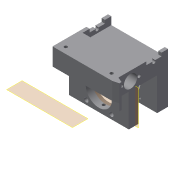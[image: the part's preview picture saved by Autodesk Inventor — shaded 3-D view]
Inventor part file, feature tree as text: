
AUTODESK INVENTOR PART (.ipt)
format: ipt  version: 2019.4 (Build 234330000, 330)  size: 334,848 bytes
history: native  units: mm
features: sketch x14, extrude x10, projected_geometry x9, hole x5, plane x4, other x3
ambient origin geometry x8: Origin, YZ Plane, XZ Plane, XY Plane, X Axis, Y Axis, Z Axis, Center Point
bodies: Body1 (feature_tree)
feature tree (45):
  plane  "Work Plane5"
  extrude  "Extrusion7"  Depth=16.0mm TaperAngle=0.0deg
  extrude  "Extrusion8"  Depth=4.0mm
  hole  "Hole1"  [1 undecoded]
  extrude  "Extrusion9"  Depth=6.2mm
  extrude  "Extrusion12"  Depth=10.0mm TaperAngle=0.0deg
  hole  "Hole4"  [1 undecoded]
  plane  "Work Plane8"
  extrude  "Extrusion13"  Depth=6.0mm
  extrude  "Extrusion18"  Depth=0.3mm
  extrude  "Extrusion19"  Depth=4.0mm
  extrude  "Extrusion20"  Depth=1.0mm
  hole  "Hole5"  [1 undecoded]
  hole  "Hole7"  [1 undecoded]
  hole  "Hole8"  [1 undecoded]
  sketch  "Sketch30"  dims[d122=6.9mm d123=2.0mm d124=0.0mm]
  plane  "Work Plane9"
  extrude  "Extrusion21"  Depth=10.0mm
  sketch  "Sketch31"  dims[d125=3.0mm d126=0.0mm d127=2.8mm d128=6.0mm d129=19.05mm d130=4.775mm d131=90.0deg d132=8.0mm d133=20.594885mm d143=4.0mm d144=6.0mm d145=19.05mm d146=4.775mm d147=90.0deg d148=8.0mm d149=20.594885mm d150=2.8mm d151=2.8mm d152=45.0mm d153=25.0mm d154=2.8mm d155=6.0mm d156=19.05mm d157=4.775mm d158=90.0deg d159=8.0mm d160=20.594885mm d161=5.0mm d162=2.0mm d163=10.0mm d164=0.0mm d165=10.0mm d166=0.0mm]
  plane  "Work Plane10"
  extrude  "Extrusion22"  Depth=10.0mm
  sketch  "Sketch7"  dims[d33=16.0mm d34=0.0mm d41=16.0mm d42=0.0mm]
  sketch  "Sketch8"  dims[d43=2.9mm d44=6.0mm d45=4.0mm d46=2.0mm d47=90.0deg d48=4.0mm d49=20.594885mm d50=24.0mm]
  sketch  "Sketch9"  dims[d51=32.0mm d52=10.0mm d53=0.0mm]
  sketch  "Sketch10"  dims[d67=6.2mm d68=6.2mm]
  projected_geometry  "Projected Loop6"
  sketch  "Sketch17"  dims[d73=7.0mm d75=10.0mm d76=0.0mm]
  sketch  "Sketch18"  dims[d77=12.0mm]
  projected_geometry  "Projected Loop7"
  sketch  "Sketch23"  dims[d85=3.5mm d86=6.0mm d87=7.0mm d88=4.0mm d89=90.0deg d90=8.0mm d91=20.594885mm d92=20.0mm]
  projected_geometry  "Projected Loop12"
  sketch  "Sketch24"  dims[d93=6.0mm d94=3.0mm d95=0.0mm d96=0.0mm d112=47.0mm]
  sketch  "Sketch25"  dims[d113=0.1mm d114=0.3mm]
  projected_geometry  "Projected Loop13"
  sketch  "Sketch26"  dims[d115=4.0mm d116=1.0mm]
  sketch  "Sketch28"  dims[d117=1.0mm d118=1.0mm]
  projected_geometry  "Projected Loop16"
  sketch  "Sketch29"  dims[d119=3.0mm d120=0.0mm d121=3.0mm]
  projected_geometry  "Projected Loop17"
  projected_geometry  "Projected Loop18"
  projected_geometry  "Projected Loop19"
  projected_geometry  "Projected Loop20"
  other  "Assembly_Opentrons_Imagingunit_v0.iam"
  other  "Assembly_spindeldrive_350mm:1"
  other  "00_spindel_bearings:1"
note: 5 required parameter values undecoded (feature->parameter linkage not recoverable at this tier; creation-order binding heuristic only, values carry confidence <= 0.55)
